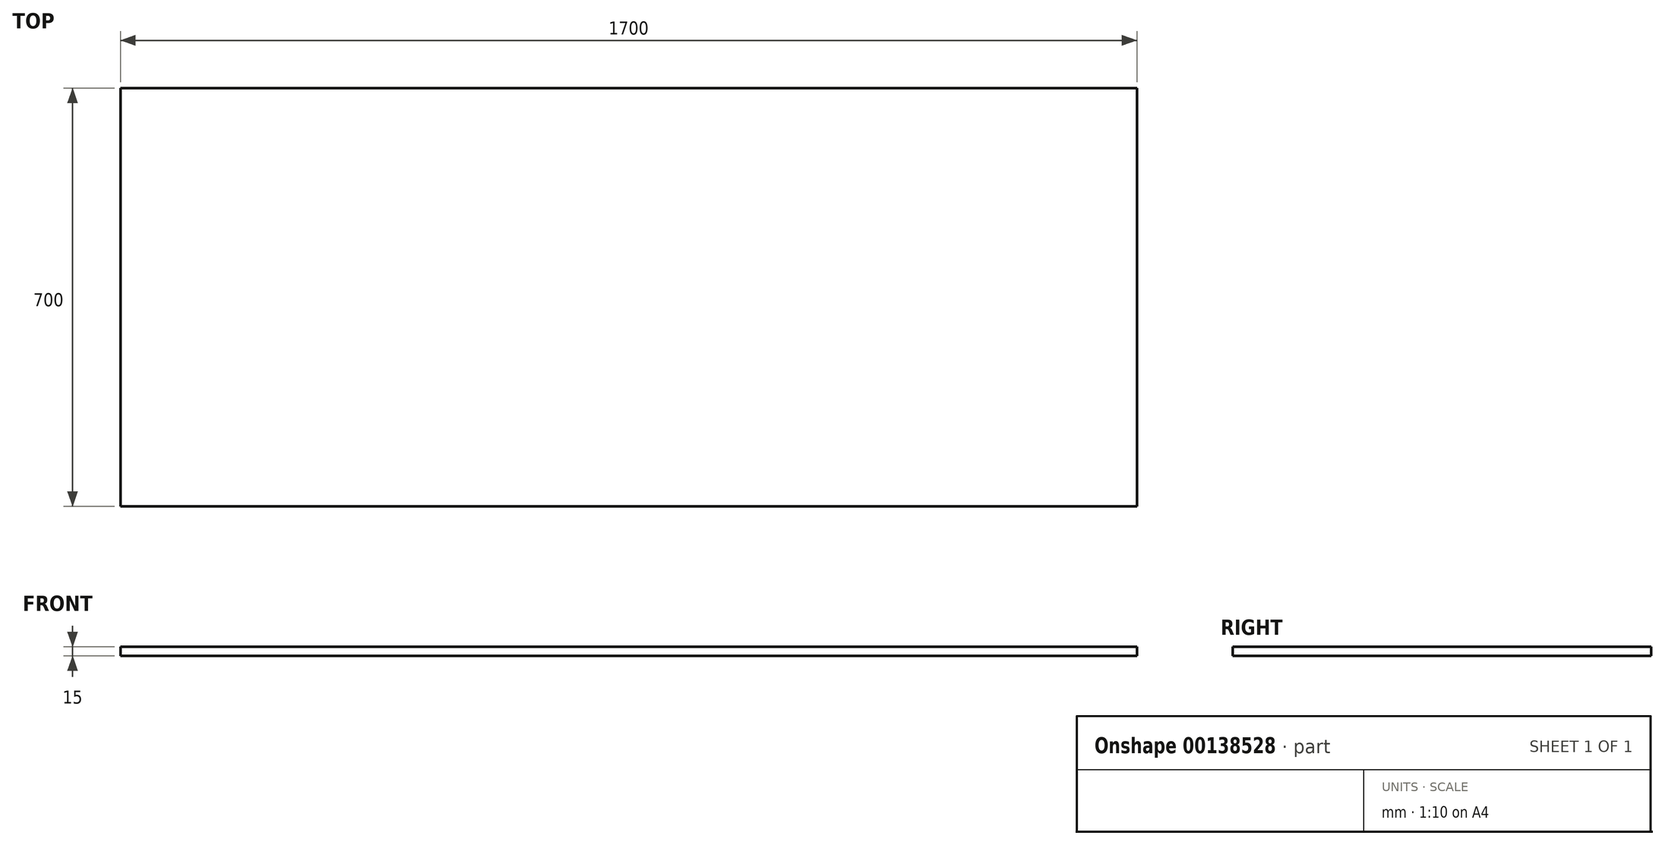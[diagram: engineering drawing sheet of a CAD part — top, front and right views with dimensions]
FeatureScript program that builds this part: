
annotation { "Feature Type Name" : "Feature", "Feature Type Description" : "" }
export const myFeature = defineFeature(function(context is Context, id is Id, definition is map)
    precondition{}
    {
        {
            var Q0;
            Q0=qCreatedBy(makeId("Right.planeOp"),FACE);
            var sketch = newSketch(context, id + "F0", { "sketchPlane" : qUnion([Q0])});
            skLineSegment(sketch, "E0.bottom", {"start": v(357.27, -7.5) * mm, "end": v(-342.73, -7.5) * mm});
            skLineSegment(sketch, "E0.top", {"start": v(357.27, 7.5) * mm, "end": v(-342.73, 7.5) * mm});
            skLineSegment(sketch, "E0.left", {"start": v(357.27, -7.5) * mm, "end": v(357.27, 7.5) * mm});
            skLineSegment(sketch, "E0.right", {"start": v(-342.73, -7.5) * mm, "end": v(-342.73, 7.5) * mm});
            skPoint(sketch, "E0.middle", {"position": v(7.27, 0) * mm});
            skSolve(sketch);
        }
        {
            var Q0;
            Q0=makeQuery(id+"F0.imprint","IMPRINT",FACE,{"disambiguationData":[TD([[makeQuery(id+"F0.imprint","IMPRINT",EDGE,{"derivedFrom":sQuery(id+"F0.wireOp",EDGE,"E0.bottom")}),-1.0]])]});
            extrude(context, id + "F1", {"entities" : qUnion([Q0]), "endBound" : BoundingType.SYMMETRIC, "depth" : 1700 * mm});
        }
    });
